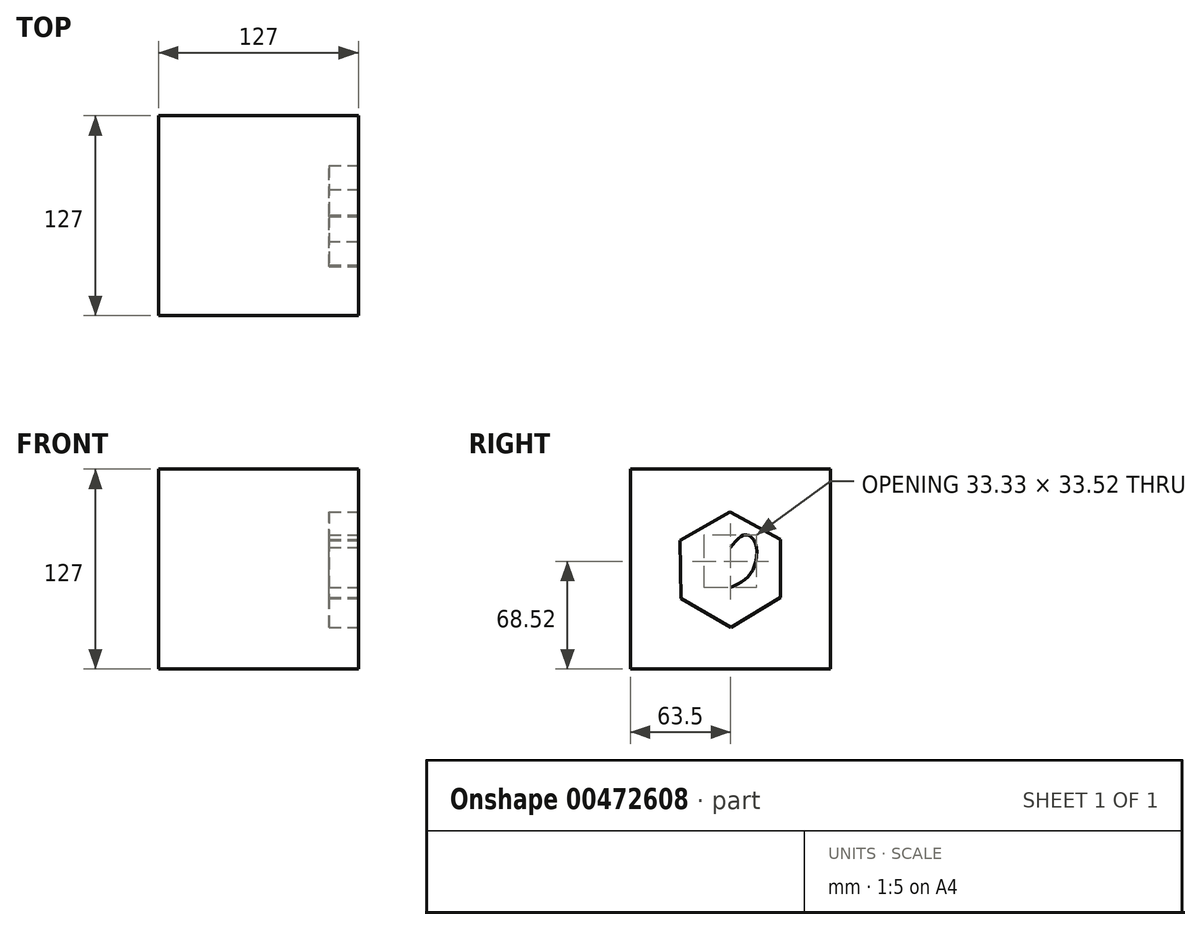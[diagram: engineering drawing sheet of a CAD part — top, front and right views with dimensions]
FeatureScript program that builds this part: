
annotation { "Feature Type Name" : "Feature", "Feature Type Description" : "" }
export const myFeature = defineFeature(function(context is Context, id is Id, definition is map)
    precondition{}
    {
        {
            var Q0;
            Q0=qCreatedBy(makeId("Right.planeOp"),FACE);
            var sketch = newSketch(context, id + "F0", { "sketchPlane" : qUnion([Q0])});
            skLineSegment(sketch, "E0.bottom", {"start": v(-63.5, 63.5) * mm, "end": v(63.5, 63.5) * mm});
            skLineSegment(sketch, "E0.top", {"start": v(-63.5, -63.5) * mm, "end": v(63.5, -63.5) * mm});
            skLineSegment(sketch, "E0.left", {"start": v(-63.5, 63.5) * mm, "end": v(-63.5, -63.5) * mm});
            skLineSegment(sketch, "E0.right", {"start": v(63.5, 63.5) * mm, "end": v(63.5, -63.5) * mm});
            skPoint(sketch, "E0.middle", {"position": v(0, 0) * mm});
            skSolve(sketch);
        }
        {
            var Q0;
            Q0 = qSketchRegion(id + "F0", true);
            extrude(context, id + "F1", {"entities" : qUnion([Q0]), "depth" : 127 * mm});
        }
        {
            var Q0;
            Q0=makeQuery(id+"F0.imprint","IMPRINT",FACE,{"disambiguationData":[TD([[makeQuery(id+"F0.imprint","IMPRINT",EDGE,{"derivedFrom":sQuery(id+"F0.wireOp",EDGE,"E0.bottom")}),-1.0]])]});
            extrude(context, id + "F2", {"entities" : qUnion([Q0]), "depth" : 127 * mm});
        }
        {
            var Q0;
            Q0=makeQuery(id+"F1.opExtrude","CAP_FACE",FACE,{"disambiguationData":[OSD([sQuery(id+"F0.wireOp",EDGE,"E0.bottom"),sQuery(id+"F0.wireOp",EDGE,"E0.top"),sQuery(id+"F0.wireOp",EDGE,"E0.left"),sQuery(id+"F0.wireOp",EDGE,"E0.right")])],"isStart":false});
            var sketch = newSketch(context, id + "F3", { "sketchPlane" : qUnion([Q0])});
            skCircle(sketch, "E1", {"center": v(0, 0) * mm, "radius": 63.5 * mm});
            skCircle(sketch, "E2.cCircle", {"center": v(0, 0) * mm, "radius": 63.5 * mm, "construction": true});
            skLineSegment(sketch, "E2.0", {"start": v(-63.5, 0) * mm, "end": v(31.75, 55) * mm});
            skLineSegment(sketch, "E2.1", {"start": v(31.75, 55) * mm, "end": v(31.75, -55) * mm});
            skLineSegment(sketch, "E2.2", {"start": v(31.75, -55) * mm, "end": v(-63.5, 0) * mm});
            skLineSegment(sketch, "E3.0", {"start": v(-32.94, 54.29) * mm, "end": v(63.48, 1.39) * mm});
            skLineSegment(sketch, "E3.1", {"start": v(63.48, 1.39) * mm, "end": v(-30.54, -55.67) * mm});
            skLineSegment(sketch, "E3.2", {"start": v(-30.54, -55.67) * mm, "end": v(-32.94, 54.29) * mm});
            skFitSpline(sketch, "E4", {"points": [v(0, -11.74) * mm, v(-13.2, -2.21) * mm, v(-15.8, 16.55) * mm, v(-9.16, 21.75) * mm, v(0, 13.66) * mm], "startDerivative": vector(-55.32, 25.42) * mm, "endDerivative": vector(38.15, -48.84) * mm});
            skFitSpline(sketch, "E5.MirrorCS", {"points": [v(0, -11.74) * mm, v(13.2, -2.21) * mm, v(15.8, 16.55) * mm, v(9.16, 21.75) * mm, v(0, 13.66) * mm], "startDerivative": vector(55.32, 25.42) * mm, "endDerivative": vector(-38.15, -48.84) * mm});
            skSolve(sketch);
        }
        {
            var Q0;
            Q0=makeQuery(id+"F3.imprint","IMPRINT",FACE,{"disambiguationData":[TD([[makeQuery(id+"F3.imprint","IMPRINT",EDGE,{"derivedFrom":sQuery(id+"F3.wireOp",EDGE,"E4")}),-1.0]])]});
            var sketch = newSketch(context, id + "F4", { "sketchPlane" : qUnion([Q0])});
            skCircle(sketch, "E6", {"center": v(0, 0) * mm, "radius": 56.7 * mm});
            skSolve(sketch);
        }
        {
            var Q0;
            Q0=makeQuery(id+"F3.imprint","IMPRINT",FACE,{"disambiguationData":[TD([[makeQuery(id+"F3.imprint","IMPRINT",EDGE,{"derivedFrom":sQuery(id+"F3.wireOp",EDGE,"E4")}),1.0]])]});
            extrude(context, id + "F5", {"entities" : qUnion([Q0]), "oppositeDirection" : true, "depth" : 18.54 * mm});
        }
    });
